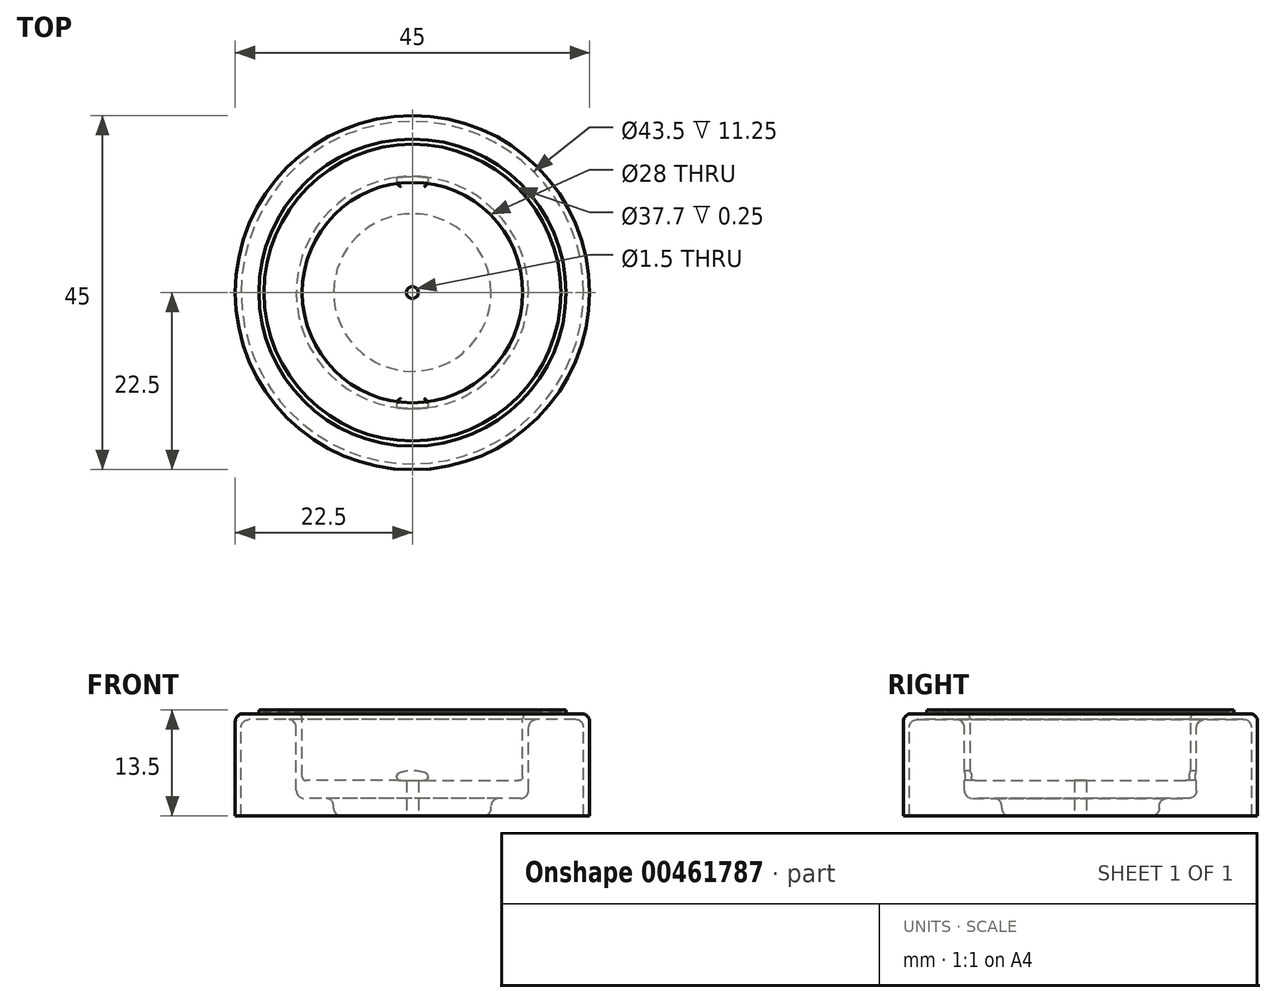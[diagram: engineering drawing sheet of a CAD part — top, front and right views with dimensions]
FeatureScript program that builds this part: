
annotation { "Feature Type Name" : "Feature", "Feature Type Description" : "" }
export const myFeature = defineFeature(function(context is Context, id is Id, definition is map)
    precondition{}
    {
        {
            var Q0;
            Q0=qCreatedBy(makeId("Right.planeOp"),FACE);
            var sketch = newSketch(context, id + "F0", { "sketchPlane" : qUnion([Q0])});
            skLineSegment(sketch, "E0", {"start": v(-45, 0) * mm, "end": v(-45, 24) * mm});
            skLineSegment(sketch, "E1", {"start": v(-43, 26) * mm, "end": v(-39, 26) * mm});
            skLineSegment(sketch, "E2", {"start": v(-39, 26) * mm, "end": v(-39, 27) * mm});
            skLineSegment(sketch, "E3", {"start": v(-39, 27) * mm, "end": v(-37.7, 27) * mm});
            skLineSegment(sketch, "E4", {"start": v(-37.7, 27) * mm, "end": v(-37.7, 26.5) * mm});
            skLineSegment(sketch, "E5", {"start": v(-37.7, 26.5) * mm, "end": v(-30, 26.5) * mm});
            skLineSegment(sketch, "E6", {"start": v(-28, 24.5) * mm, "end": v(-28, 10) * mm});
            skLineSegment(sketch, "E7", {"start": v(-27, 9) * mm, "end": v(0, 9) * mm});
            skLineSegment(sketch, "E8", {"start": v(-45, 0) * mm, "end": v(-43.5, 0) * mm});
            skLineSegment(sketch, "E9", {"start": v(-43.5, 0) * mm, "end": v(-43.5, 22.5) * mm});
            skLineSegment(sketch, "E10", {"start": v(-41.5, 24.5) * mm, "end": v(-31.5, 24.5) * mm});
            skLineSegment(sketch, "E11", {"start": v(-29.5, 22.5) * mm, "end": v(-29.5, 6.5) * mm});
            skLineSegment(sketch, "E12", {"start": v(-27.5, 4.5) * mm, "end": v(-22, 4.5) * mm});
            skLineSegment(sketch, "E13", {"start": v(-20, 2.5) * mm, "end": v(-20, 2) * mm});
            skLineSegment(sketch, "E14", {"start": v(0, 0) * mm, "end": v(-18, 0) * mm});
            skPoint(sketch, "E15.visualSharp", {"position": v(-43.5, 24.5) * mm});
            skArc(sketch, "E15.filletArc", {"start": v(-41.5, 24.5) * mm, "mid": v(-42.91, 23.91) * mm, "end": v(-43.5, 22.5) * mm});
            skPoint(sketch, "E16.visualSharp", {"position": v(-45, 26) * mm});
            skArc(sketch, "E16.filletArc", {"start": v(-43, 26) * mm, "mid": v(-44.41, 25.41) * mm, "end": v(-45, 24) * mm});
            skPoint(sketch, "E17.visualSharp", {"position": v(-29.5, 24.5) * mm});
            skArc(sketch, "E17.filletArc", {"start": v(-29.5, 22.5) * mm, "mid": v(-30.09, 23.91) * mm, "end": v(-31.5, 24.5) * mm});
            skPoint(sketch, "E18.visualSharp", {"position": v(-28, 26.5) * mm});
            skArc(sketch, "E18.filletArc", {"start": v(-28, 24.5) * mm, "mid": v(-28.59, 25.91) * mm, "end": v(-30, 26.5) * mm});
            skPoint(sketch, "E19.visualSharp", {"position": v(-29.5, 4.5) * mm});
            skArc(sketch, "E19.filletArc", {"start": v(-29.5, 6.5) * mm, "mid": v(-28.91, 5.09) * mm, "end": v(-27.5, 4.5) * mm});
            skPoint(sketch, "E20.visualSharp", {"position": v(-20, 0) * mm});
            skArc(sketch, "E20.filletArc", {"start": v(-20, 2) * mm, "mid": v(-19.41, 0.59) * mm, "end": v(-18, 0) * mm});
            skPoint(sketch, "E21.visualSharp", {"position": v(-20, 4.5) * mm});
            skArc(sketch, "E21.filletArc", {"start": v(-20, 2.5) * mm, "mid": v(-20.59, 3.91) * mm, "end": v(-22, 4.5) * mm});
            skPoint(sketch, "E22.visualSharp", {"position": v(-28, 9) * mm});
            skArc(sketch, "E22.filletArc", {"start": v(-28, 10) * mm, "mid": v(-27.7, 9.3) * mm, "end": v(-27, 9) * mm});
            skLineSegment(sketch, "E23", {"start": v(0, 9) * mm, "end": v(0, 0) * mm});
            skSolve(sketch);
        }
        {
            var Q0;
            Q0=qSketchRegion(id+"F0",true);
            var Q1;
            Q1=sQuery(id+"F0.wireOp",EDGE,"E23");
            revolve(context, id + "F1", {"entities" : qUnion([Q0]), "axis" : qUnion([Q1]), "revolveType" : RevolveType.FULL});
        }
        {
            var Q0;
            Q0=qCreatedBy(makeId("Top.planeOp"),FACE);
            var sketch = newSketch(context, id + "F2", { "sketchPlane" : qUnion([Q0])});
            skCircle(sketch, "E24", {"center": v(0, 0) * mm, "radius": 1.5 * mm});
            skSolve(sketch);
        }
        {
            var Q0;
            Q0=qSketchRegion(id+"F2",true);
            extrude(context, id + "F3", {"entities" : qUnion([Q0]), "operationType" : NewBodyOperationType.REMOVE, "depth" : 25 * mm});
        }
        {
            var Q0;
            Q0=qCreatedBy(makeId("Front.planeOp"),FACE);
            var sketch = newSketch(context, id + "F4", { "sketchPlane" : qUnion([Q0])});
            skLineSegment(sketch, "E25", {"start": v(3, 9) * mm, "end": v(0, 9) * mm});
            skArc(sketch, "E26", {"start": v(3, 9) * mm, "mid": v(3.99, 9.84) * mm, "end": v(3.32, 10.95) * mm});
            skLineSegment(sketch, "E27", {"start": v(0, 11) * mm, "end": v(0, 9) * mm, "construction": true});
            skLineSegment(sketch, "E28.MirrorCS", {"start": v(-3, 9) * mm, "end": v(0, 9) * mm});
            skArc(sketch, "E29.MirrorCS", {"start": v(-3, 9) * mm, "mid": v(-3.99, 9.84) * mm, "end": v(-3.32, 10.95) * mm});
            skArc(sketch, "E30", {"start": v(3.32, 10.95) * mm, "mid": v(0, 11.5) * mm, "end": v(-3.32, 10.95) * mm});
            skSolve(sketch);
        }
        {
            var Q0;
            Q0=qSketchRegion(id+"F4",true);
            var Q1;
            Q1=makeQuery(id+"F1.opRevolve","SWEPT_FACE",FACE,{"disambiguationData":[OSD([sQuery(id+"F0.wireOp",EDGE,"E9")])]});
            var Q2;
            Q2=makeQuery(id+"F1.opRevolve","SWEPT_FACE",FACE,{"disambiguationData":[OSD([sQuery(id+"F0.wireOp",EDGE,"E9")])]});
            extrude(context, id + "F5", {"entities" : qUnion([Q0]), "operationType" : NewBodyOperationType.REMOVE, "endBound" : BoundingType.UP_TO_SURFACE, "oppositeDirection" : true, "endBoundEntityFace" : qUnion([Q1]), "depth" : 25 * mm, "hasSecondDirection" : true, "secondDirectionBound" : SecondDirectionBoundingType.UP_TO_SURFACE, "secondDirectionOppositeDirection" : false, "secondDirectionBoundEntityFace" : qUnion([Q2]), "secondDirectionDepth" : 25 * mm});
        }
        {
            var Q0;
            Q0=makeQuery(id+"F1.opRevolve","SWEPT_BODY",BODY,{"disambiguationData":[OSD([sQuery(id+"F0.wireOp",EDGE,"E0"),sQuery(id+"F0.wireOp",EDGE,"E1"),sQuery(id+"F0.wireOp",EDGE,"E2"),sQuery(id+"F0.wireOp",EDGE,"E3"),sQuery(id+"F0.wireOp",EDGE,"E4"),sQuery(id+"F0.wireOp",EDGE,"E5"),sQuery(id+"F0.wireOp",EDGE,"E6"),sQuery(id+"F0.wireOp",EDGE,"E7"),sQuery(id+"F0.wireOp",EDGE,"E8"),sQuery(id+"F0.wireOp",EDGE,"E9"),sQuery(id+"F0.wireOp",EDGE,"E10"),sQuery(id+"F0.wireOp",EDGE,"E11"),sQuery(id+"F0.wireOp",EDGE,"E12"),sQuery(id+"F0.wireOp",EDGE,"E13"),sQuery(id+"F0.wireOp",EDGE,"E14"),sQuery(id+"F0.wireOp",EDGE,"E15.filletArc"),sQuery(id+"F0.wireOp",EDGE,"E16.filletArc"),sQuery(id+"F0.wireOp",EDGE,"E17.filletArc"),sQuery(id+"F0.wireOp",EDGE,"E18.filletArc"),sQuery(id+"F0.wireOp",EDGE,"E19.filletArc"),sQuery(id+"F0.wireOp",EDGE,"E20.filletArc"),sQuery(id+"F0.wireOp",EDGE,"E21.filletArc"),sQuery(id+"F0.wireOp",EDGE,"E22.filletArc"),sQuery(id+"F0.wireOp",EDGE,"E23")])]});
            var Q1;
            Q1=qCreatedBy(makeId("Origin.pointOp"),VERTEX);
            transform(context, id + "F6", {"entities" : qUnion([Q0]), "transformType" : TransformType.SCALE_UNIFORMLY, "scale" : 0.5, "scalePoint" : qUnion([Q1]), "makeCopy" : false});
        }
    });
